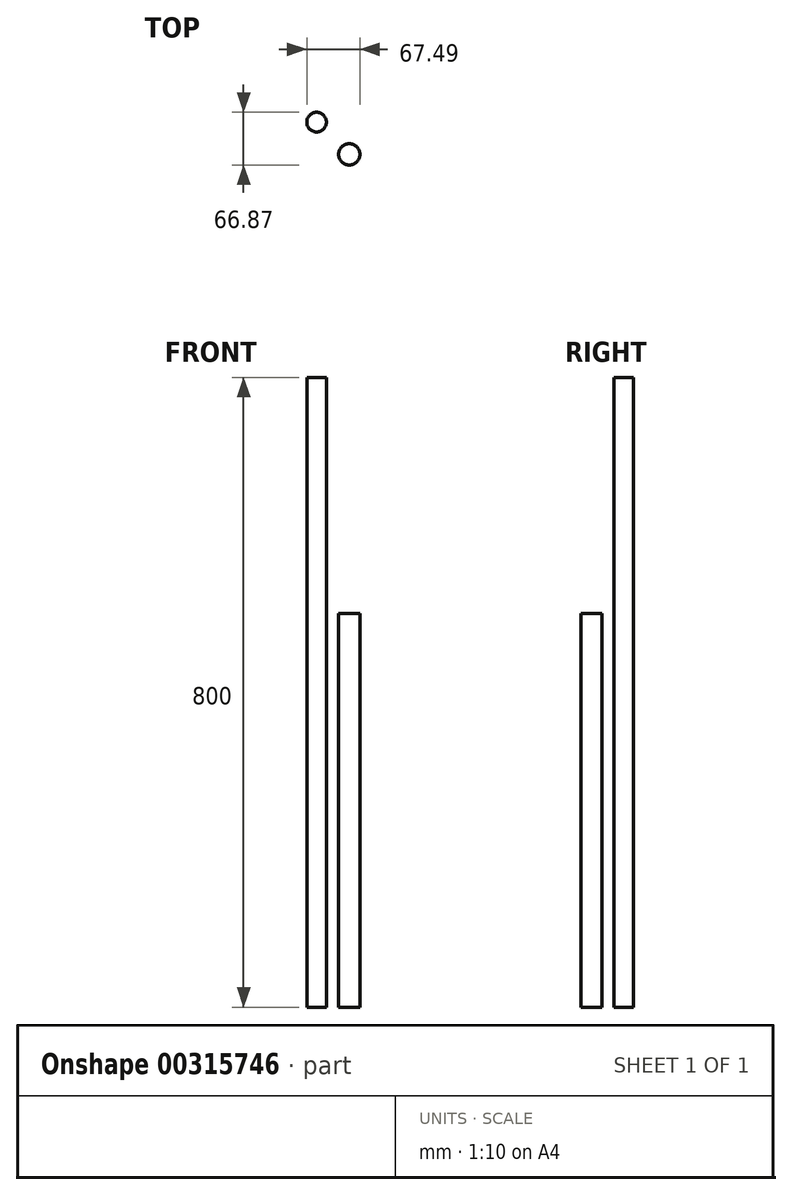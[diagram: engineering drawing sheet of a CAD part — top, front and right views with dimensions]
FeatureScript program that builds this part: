
annotation { "Feature Type Name" : "Feature", "Feature Type Description" : "" }
export const myFeature = defineFeature(function(context is Context, id is Id, definition is map)
    precondition{}
    {
        {
            var Q0;
            Q0=qCreatedBy(makeId("Top.planeOp"),FACE);
            var sketch = newSketch(context, id + "F0", { "sketchPlane" : qUnion([Q0])});
            skCircle(sketch, "E0", {"center": v(0, 0) * mm, "radius": 12.5 * mm});
            skSolve(sketch);
        }
        {
            var Q0;
            Q0=makeQuery(id+"F0.imprint","IMPRINT",FACE,{"disambiguationData":[TD([[makeQuery(id+"F0.imprint","IMPRINT",EDGE,{"derivedFrom":sQuery(id+"F0.wireOp",EDGE,"E0")}),1.0]])]});
            extrude(context, id + "F1", {"entities" : qUnion([Q0]), "depth" : 800 * mm});
        }
        {
            var Q0;
            Q0=qCreatedBy(makeId("Top.planeOp"),FACE);
            var sketch = newSketch(context, id + "F2", { "sketchPlane" : qUnion([Q0])});
            skCircle(sketch, "E1", {"center": v(41.49, -40.87) * mm, "radius": 13.5 * mm});
            skSolve(sketch);
        }
        {
            var Q0;
            Q0=makeQuery(id+"F2.imprint","IMPRINT",FACE,{"disambiguationData":[TD([[makeQuery(id+"F2.imprint","IMPRINT",EDGE,{"derivedFrom":sQuery(id+"F2.wireOp",EDGE,"E1")}),1.0]])]});
            extrude(context, id + "F3", {"entities" : qUnion([Q0]), "depth" : 500 * mm});
        }
    });
